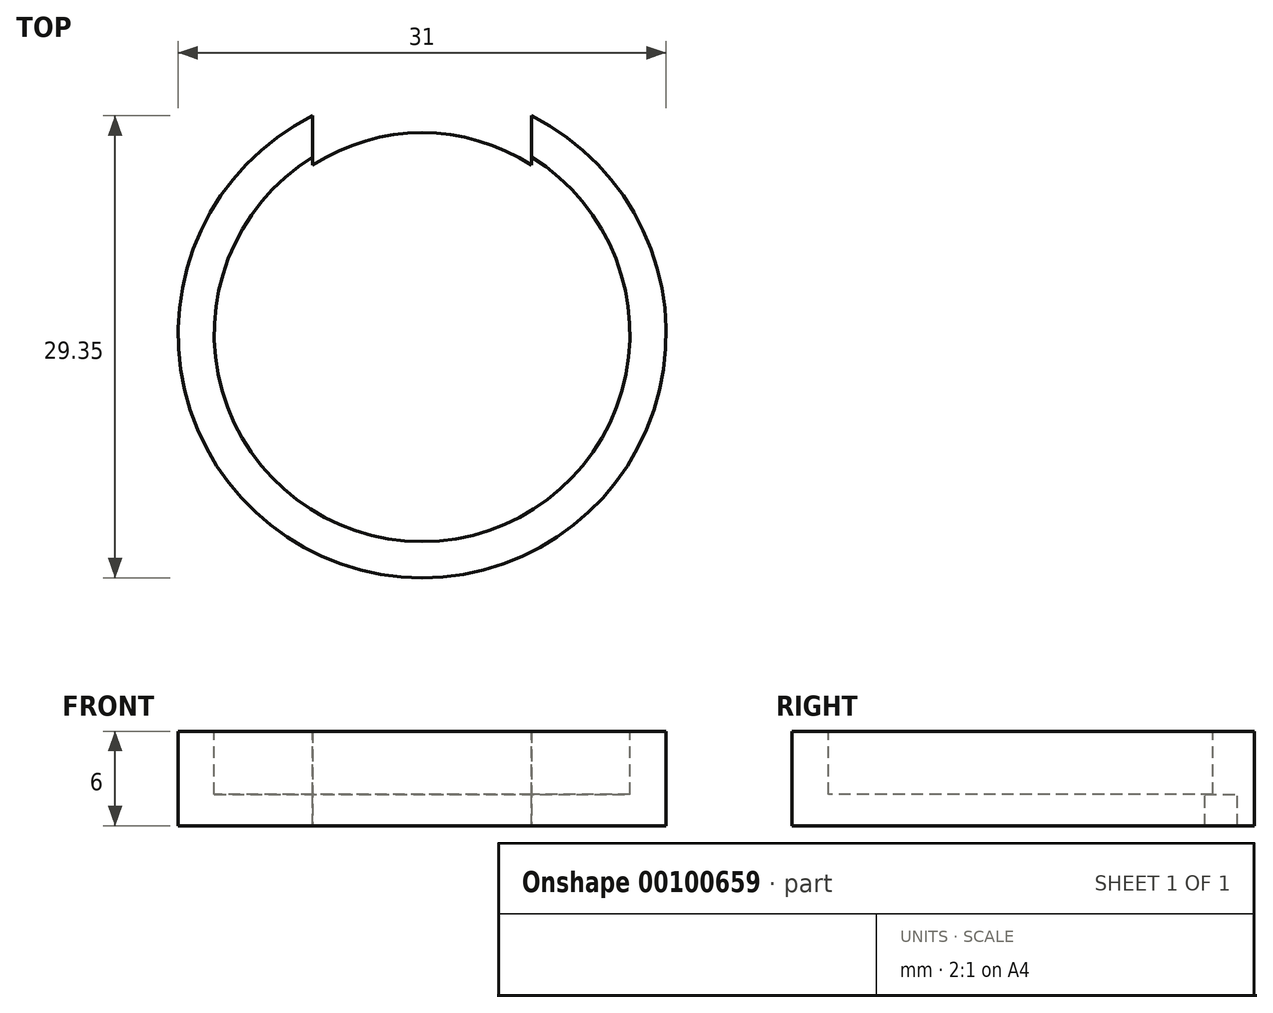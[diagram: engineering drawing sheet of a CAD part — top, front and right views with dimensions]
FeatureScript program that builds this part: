
annotation { "Feature Type Name" : "Feature", "Feature Type Description" : "" }
export const myFeature = defineFeature(function(context is Context, id is Id, definition is map)
    precondition{}
    {
        {
            var Q0;
            Q0=qCreatedBy(makeId("Top.planeOp"),FACE);
            var sketch = newSketch(context, id + "F0", { "sketchPlane" : qUnion([Q0])});
            skCircle(sketch, "E0", {"center": v(0, 0) * mm, "radius": 15.5 * mm});
            skSolve(sketch);
        }
        {
            var Q0;
            Q0=qSketchRegion(id+"F0",true);
            extrude(context, id + "F1", {"entities" : qUnion([Q0]), "depth" : 6 * mm, "offsetDistance" : 25 * mm});
        }
        {
            var Q0;
            Q0=makeQuery(id+"F1.opExtrude","CAP_FACE",FACE,{"disambiguationData":[OSD([sQuery(id+"F0.wireOp",EDGE,"E0")])],"isStart":false});
            var sketch = newSketch(context, id + "F2", { "sketchPlane" : qUnion([Q0])});
            skCircle(sketch, "E1", {"center": v(0, 0) * mm, "radius": 13.2 * mm});
            skSolve(sketch);
        }
        {
            var Q0;
            Q0=qSketchRegion(id+"F2",true);
            extrude(context, id + "F3", {"entities" : qUnion([Q0]), "operationType" : NewBodyOperationType.REMOVE, "oppositeDirection" : true, "depth" : 4 * mm, "offsetDistance" : 25 * mm});
        }
        {
            var Q0;
            Q0=makeQuery(id+"F1.opExtrude","CAP_FACE",FACE,{"disambiguationData":[OSD([sQuery(id+"F0.wireOp",EDGE,"E0")])],"isStart":false});
            var sketch = newSketch(context, id + "F4", { "sketchPlane" : qUnion([Q0])});
            skLineSegment(sketch, "E2.bottom", {"start": v(-6.95, 21.57) * mm, "end": v(6.95, 21.57) * mm});
            skLineSegment(sketch, "E2.left", {"start": v(-6.95, 21.57) * mm, "end": v(-6.95, 10.71) * mm});
            skLineSegment(sketch, "E2.right", {"start": v(6.95, 21.57) * mm, "end": v(6.95, 10.71) * mm});
            skArc(sketch, "E3", {"start": v(-6.95, 10.71) * mm, "mid": v(0, 12.77) * mm, "end": v(6.95, 10.71) * mm});
            skSolve(sketch);
        }
        {
            var Q0;
            Q0=qSketchRegion(id+"F4",true);
            extrude(context, id + "F5", {"entities" : qUnion([Q0]), "operationType" : NewBodyOperationType.REMOVE, "oppositeDirection" : true, "depth" : 25 * mm, "offsetDistance" : 25 * mm});
        }
    });
